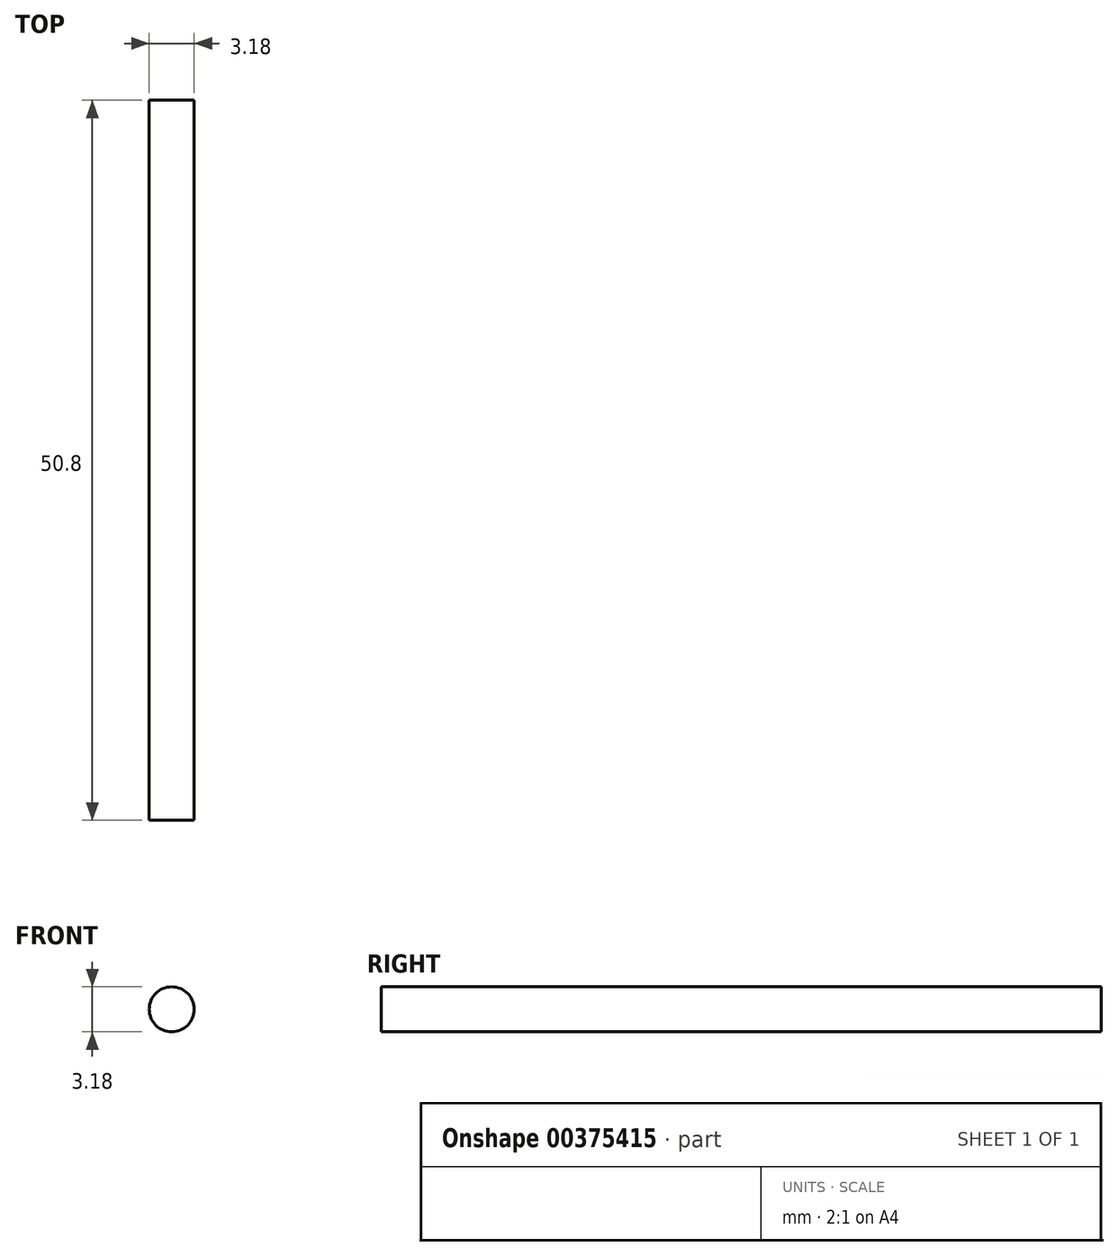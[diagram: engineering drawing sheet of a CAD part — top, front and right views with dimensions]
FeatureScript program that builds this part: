
annotation { "Feature Type Name" : "Feature", "Feature Type Description" : "" }
export const myFeature = defineFeature(function(context is Context, id is Id, definition is map)
    precondition{}
    {
        {
            var Q0;
            Q0=qCreatedBy(makeId("Front.planeOp"),FACE);
            var sketch = newSketch(context, id + "F0", { "sketchPlane" : qUnion([Q0])});
            skCircle(sketch, "E0", {"center": v(0, 0) * mm, "radius": 1.59 * mm});
            skSolve(sketch);
        }
        {
            var Q0;
            Q0=qSketchRegion(id+"F0",true);
            extrude(context, id + "F1", {"entities" : qUnion([Q0]), "depth" : 50.8 * mm, "symmetric" : true});
        }
    });
